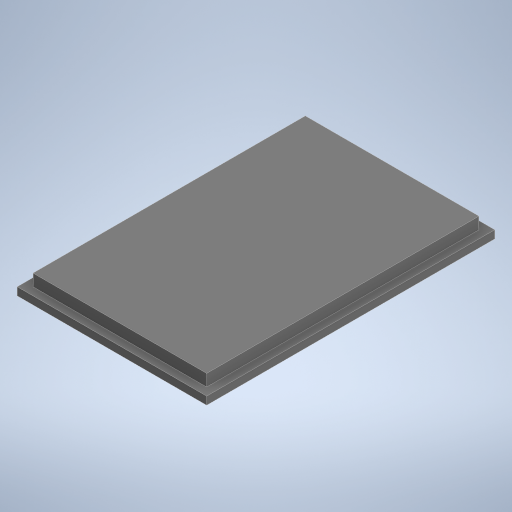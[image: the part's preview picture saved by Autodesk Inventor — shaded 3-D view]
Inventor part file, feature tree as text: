
AUTODESK INVENTOR PART (.ipt)
format: ipt  version: 2023 (Build 270158000, 158)  size: 219,136 bytes
history: native  units: in
note: dims shown in document units (in); Inventor stores cm internally (conversion verified against a paired STEP export)
features: extrude x2, sketch x1
ambient origin geometry x8: Origin, YZ Plane, XZ Plane, XY Plane, X Axis, Y Axis, Z Axis, Center Point
bodies: Solid1 (feature_tree)
feature tree (3):
  sketch  "Sketch1"  dims[d0=2.2in d1=3.45in d2=0.1in d3=0.25in d4=0.0in d5=0.1in d6=0.0in]
  extrude  "Extrusion1"  Depth=3.45in
  extrude  "Extrusion2"  Depth=0.1in
